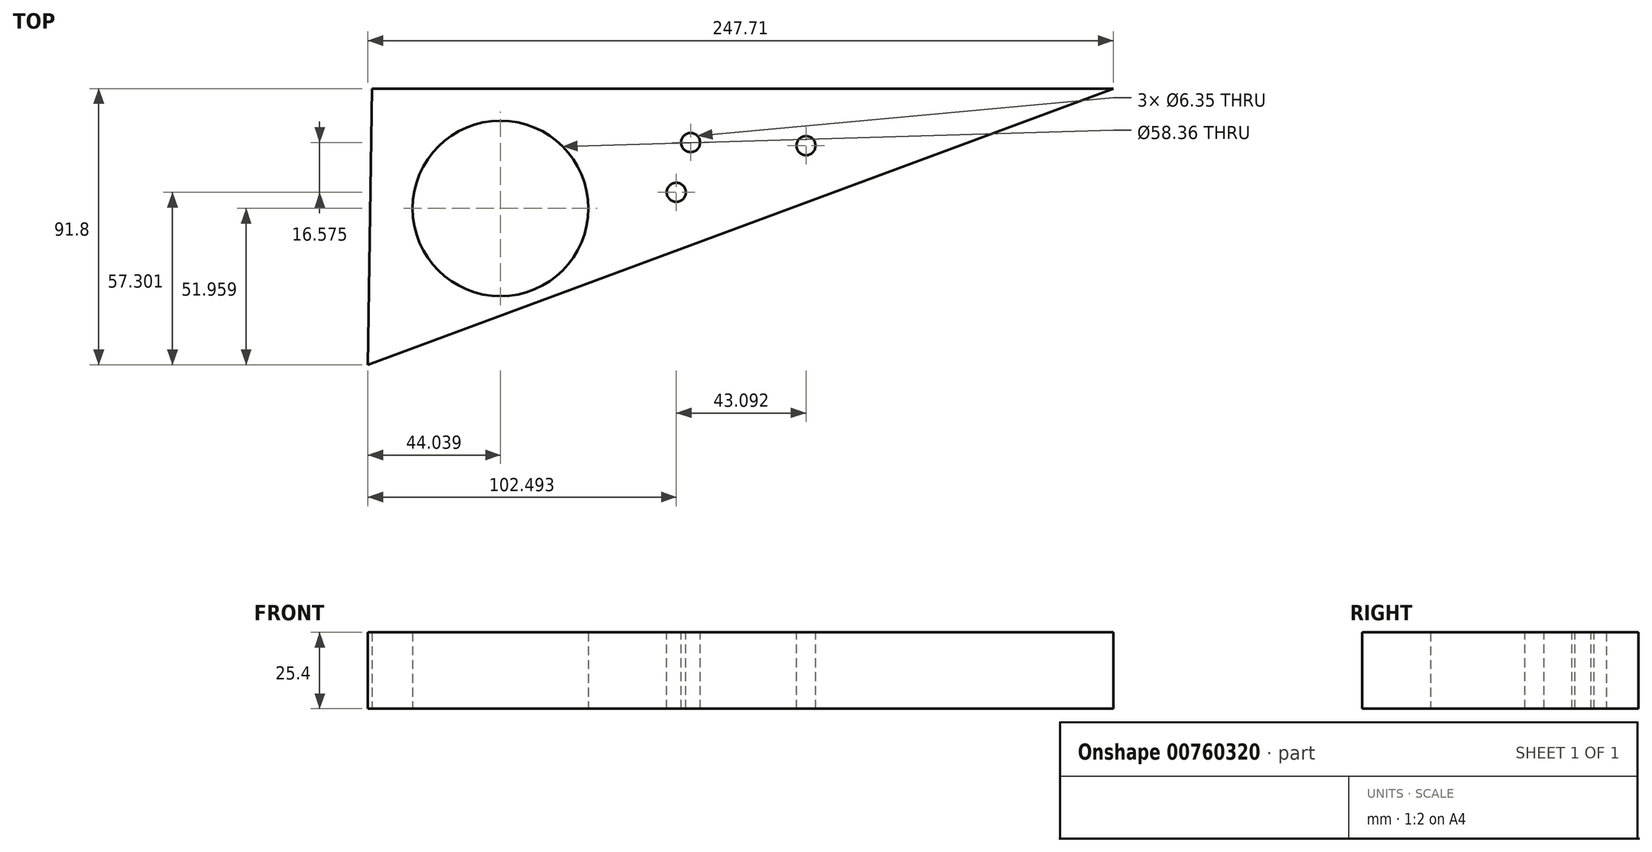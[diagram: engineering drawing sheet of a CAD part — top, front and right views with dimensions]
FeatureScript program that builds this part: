
annotation { "Feature Type Name" : "Feature", "Feature Type Description" : "" }
export const myFeature = defineFeature(function(context is Context, id is Id, definition is map)
    precondition{}
    {
        {
            var Q0;
            Q0=qCreatedBy(makeId("Top.planeOp"),FACE);
            var sketch = newSketch(context, id + "F0", { "sketchPlane" : qUnion([Q0])});
            skLineSegment(sketch, "E0", {"start": v(-85.1, 0) * mm, "end": v(161.24, 0) * mm});
            skLineSegment(sketch, "E1", {"start": v(161.24, 0) * mm, "end": v(-86.47, -91.8) * mm});
            skLineSegment(sketch, "E2", {"start": v(-86.47, -91.8) * mm, "end": v(-85.1, 0) * mm});
            skCircle(sketch, "E3", {"center": v(-42.43, -39.84) * mm, "radius": 29.18 * mm});
            skPoint(sketch, "E4", {"position": v(25.52, -38.52) * mm});
            skPoint(sketch, "E5", {"position": v(0, -23.38) * mm});
            skPoint(sketch, "E6", {"position": v(81.94, -17.88) * mm});
            skSolve(sketch);
        }
        {
            var Q0;
            Q0=makeQuery(id+"F0.imprint","IMPRINT",FACE,{"disambiguationData":[TD([[makeQuery(id+"F0.imprint","IMPRINT",EDGE,{"derivedFrom":sQuery(id+"F0.wireOp",EDGE,"E0")}),-1.0]])]});
            extrude(context, id + "F1", {"entities" : qUnion([Q0]), "depth" : 25.4 * mm, "offsetDistance" : 25.4 * mm});
        }
        {
            var Q0;
            Q0=makeQuery(id+"F1.opExtrude","CAP_FACE",FACE,{"disambiguationData":[OSD([sQuery(id+"F0.wireOp",EDGE,"E0"),sQuery(id+"F0.wireOp",EDGE,"E1"),sQuery(id+"F0.wireOp",EDGE,"E2"),sQuery(id+"F0.wireOp",EDGE,"E3")])],"isStart":false});
            var sketch = newSketch(context, id + "F2", { "sketchPlane" : qUnion([Q0])});
            skPoint(sketch, "E7", {"position": v(16.02, -34.5) * mm});
            skPoint(sketch, "E8", {"position": v(59.11, -18.97) * mm});
            skPoint(sketch, "E9", {"position": v(20.76, -17.92) * mm});
            skSolve(sketch);
        }
        {
            var Q0;
            Q0=sQuery(id+"F2.wireOp",VERTEX,"E9");
            var Q1;
            Q1=sQuery(id+"F2.wireOp",VERTEX,"E7");
            var Q2;
            Q2=sQuery(id+"F2.wireOp",VERTEX,"E8");
            var Q3;
            Q3=makeQuery(id+"F1.opExtrude","SWEPT_BODY",BODY,{"disambiguationData":[OSD([sQuery(id+"F0.wireOp",EDGE,"E0"),sQuery(id+"F0.wireOp",EDGE,"E1"),sQuery(id+"F0.wireOp",EDGE,"E2"),sQuery(id+"F0.wireOp",EDGE,"E3")])]});
            hole(context, id + "F3", {"style" : HoleStyle.SIMPLE, "endStyle" : HoleEndStyle.THROUGH, "holeDiameter" : 6.35 * mm, "majorDiameter" : 6.35 * mm, "isTappedThrough" : true, "tappedDepth" : 12.7 * mm, "tapClearance" : 3, "locations" : qUnion([Q0, Q1, Q2]), "scope" : qUnion([Q3])});
        }
    });
